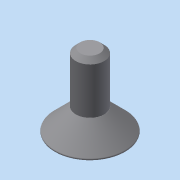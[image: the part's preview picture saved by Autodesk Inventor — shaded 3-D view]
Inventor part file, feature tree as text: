
AUTODESK INVENTOR PART (.ipt)
format: ipt  version: 2014 (Build 180170000, 170)  size: 100,352 bytes
history: native  units: in
note: dims shown in document units (in); Inventor stores cm internally (conversion verified against a paired STEP export)
features: extrude x2, chamfer x2, sketch x2, fillet x1
ambient origin geometry x8: Origin, YZ Plane, XZ Plane, XY Plane, X Axis, Y Axis, Z Axis, Center Point
bodies: Solid1 (feature_tree)
feature tree (7):
  extrude  "Extrusion1"  Depth=0.225in TaperAngle=0.0deg
  extrude  "Extrusion2"  Depth=0.1in TaperAngle=0.0deg
  chamfer  "Chamfer1"  Distance=0.1in Angle=45.0deg
  fillet  "Fillet1"  Radius=0.005in
  chamfer  "Chamfer2"  Distance=0.02in Angle=45.0deg
  sketch  "Sketch1"  dims[d0=0.126in d1=0.225in d2=0.0in]
  sketch  "Sketch2"  dims[d3=0.327in d4=0.1in d5=0.0in d6=0.1in d7=0.125in d8=45.0deg d9=0.005in d10=0.02in d11=0.125in d12=45.0deg]
